# Revit family: Crealco Skyline Heavy Duty Sash Top Hung I
name_source: partatom
category: Windows
revit_build: Autodesk Revit 2014 (Build: 20130308_1515(x64)
units: mm (PartAtom-declared; Revit-internal decimal feet)

## types (24) — shared parameters
Corrected Mullion Configuration = 2 mm  [stored 0.00656168 ft]
Custom Sash Height = 525 mm
Description = Top Hung Type I Standard Sash Window
Frame Profile Thickness = 41 mm  [stored 0.134514 ft]
Heavy Duty Sash = Yes
Limit Fixed Pane Height Max = 3300 mm  [stored 10.8268 ft]
Limit Fixed Pane Height Min = 200 mm  [stored 0.656168 ft]
Limit Fixed Pane Width Max = 3000 mm  [stored 9.84252 ft]
Limit Fixed Pane Width Min = 200 mm  [stored 0.656168 ft]
Limit Sash Height Max = 1200 mm  [stored 3.93701 ft]
Limit Sash Height Min = 300 mm  [stored 0.984252 ft]
Limit Sash Width Max = 1500 mm  [stored 4.92126 ft]
Limit Sash Width Min = 300 mm  [stored 0.984252 ft]
Manufacturer = Crealco
Max System DG Unit Thickness = 25 mm  [stored 0.082021 ft]
Model = Skyline
Rough Width = 3 mm  [stored 0.00984252 ft]
Sash Side Gap = 44 mm
Standard Mullion Different = No
Standard Sash = No
URL = www.crealco.co.za
Wall Closure = By host
zero-valued in all types: Custom Frame Offset From Exterior

## per-type parameters (varying)
| type | Clearvue Insulated LowE SHGC Value | Clearvue Insulated LowE U Value | Clearvue Insulated SHGC Value | Clearvue Insulated U Value | Clearvue SHGC Value | Clearvue U Value | Custom Sash Width | Custom Windload | Custom Window Height | Custom Window Width | Energy Advantage SHGC Value | Energy Advantage U Value | Intruderprufe Insulated LowE SHGC Value | Intruderprufe Insulated LowE U Value | Intruderprufe Insulated SHGC Value | Intruderprufe Insulated U Value | Intruderprufe LowE SHGC Value | Intruderprufe LowE U Value | Intruderprufe SHGC Value | Intruderprufe U Value | Toughened Safety SHGC Value | Toughened Safety U Value |
| 1200 x 1500mm 1000Pa | 0.696 | 4.39 | 0.696 | 4.48 | 0.557 | 6.06 | 525 mm | 1000 mm  [stored 3.28084 ft] | 1490 mm  [stored 4.88845 ft] | 1190 mm  [stored 3.9042 ft] | 0.5 | 4.71 | 0.578 | 3.25 | 0.579 | 3.45 | 0.465 | 4.55 | 0.524 | 5.78 | 0.557 | 6.06 |
| 1200 x 1500mm 1500Pa | 0.696 | 4.39 | 0.696 | 4.48 | 0.557 | 6.06 | 525 mm | 1500 mm  [stored 4.92126 ft] | 1490 mm  [stored 4.88845 ft] | 1190 mm  [stored 3.9042 ft] | 0.5 | 4.71 | 0.578 | 3.25 | 0.579 | 3.45 | 0.465 | 4.55 | 0.524 | 5.78 | 0.557 | 6.06 |
| 1200 x 1500mm 2000Pa | 0.697 | 4.52 | 0.697 | 4.61 | 0.549 | 6.12 | 525 mm | 2000 mm  [stored 6.56168 ft] | 1490 mm  [stored 4.88845 ft] | 1190 mm  [stored 3.9042 ft] | 0.493 | 4.81 | 0.58 | 3.38 | 0.58 | 3.58 | 0.458 | 4.65 | 0.516 | 5.84 | 0.549 | 6.12 |
| 1500 x 1500mm 2000Pa | 0.728 | 4.69 | 0.728 | 4.76 | 0.597 | 6.08 | 525 mm | 2000 mm  [stored 6.56168 ft] | 1490 mm  [stored 4.88845 ft] | 1490 mm  [stored 4.88845 ft] | 0.535 | 4.64 | 0.605 | 3.37 | 0.605 | 3.53 | 0.497 | 4.48 | 0.561 | 5.82 | 0.597 | 6.08 |
| 1500 x 1500mm 1000Pa | 0.727 | 4.59 | 0.727 | 4.66 | 0.604 | 6.03 | 525 mm | 1000 mm  [stored 3.28084 ft] | 1490 mm  [stored 4.88845 ft] | 1490 mm  [stored 4.88845 ft] | 0.541 | 4.56 | 0.604 | 3.27 | 0.605 | 3.42 | 0.503 | 4.41 | 0.568 | 5.77 | 0.604 | 6.03 |
| 1500 x 1500mm 1500Pa | 0.727 | 4.59 | 0.727 | 4.66 | 0.604 | 6.03 | 525 mm | 1500 mm  [stored 4.92126 ft] | 1490 mm  [stored 4.88845 ft] | 1490 mm  [stored 4.88845 ft] | 0.541 | 4.56 | 0.604 | 3.27 | 0.605 | 3.42 | 0.503 | 4.41 | 0.568 | 5.77 | 0.604 | 6.03 |
| 1200 x 1800mm 1000Pa | 0.71 | 4.48 | 0.71 | 4.57 | 0.582 | 6.04 | 525 mm | 1000 mm  [stored 3.28084 ft] | 1790 mm  [stored 5.8727 ft] | 1190 mm  [stored 3.9042 ft] | 0.522 | 4.64 | 0.59 | 3.28 | 0.591 | 3.45 | 0.485 | 4.48 | 0.547 | 5.77 | 0.582 | 6.04 |
| 1200 x 1800mm 1500Pa | 0.711 | 4.62 | 0.711 | 4.7 | 0.569 | 6.12 | 525 mm | 1500 mm  [stored 4.92126 ft] | 1790 mm  [stored 5.8727 ft] | 1190 mm  [stored 3.9042 ft] | 0.511 | 4.76 | 0.591 | 3.41 | 0.592 | 3.57 | 0.475 | 4.59 | 0.535 | 5.84 | 0.569 | 6.12 |
| 1200 x 1800mm 2000Pa | 0.711 | 4.62 | 0.711 | 4.7 | 0.569 | 6.12 | 525 mm | 2000 mm  [stored 6.56168 ft] | 1790 mm  [stored 5.8727 ft] | 1190 mm  [stored 3.9042 ft] | 0.511 | 4.76 | 0.591 | 3.41 | 0.592 | 3.57 | 0.475 | 4.59 | 0.535 | 5.84 | 0.569 | 6.12 |
| 1500 x 1800mm 1000Pa | 0.739 | 4.79 | 0.739 | 4.86 | 0.615 | 6.08 | 525 mm | 1000 mm  [stored 3.28084 ft] | 1790 mm  [stored 5.8727 ft] | 1490 mm  [stored 4.88845 ft] | 0.551 | 4.59 | 0.614 | 3.4 | 0.615 | 3.53 | 0.512 | 4.43 | 0.578 | 5.82 | 0.615 | 6.08 |
| 1500 x 1800mm 1500Pa | 0.739 | 4.79 | 0.739 | 4.86 | 0.615 | 6.08 | 525 mm | 1500 mm  [stored 4.92126 ft] | 1790 mm  [stored 5.8727 ft] | 1490 mm  [stored 4.88845 ft] | 0.551 | 4.59 | 0.614 | 3.4 | 0.615 | 3.53 | 0.512 | 4.43 | 0.578 | 5.82 | 0.615 | 6.08 |
| 1500 x 1800mm 2000Pa | 0.739 | 4.79 | 0.739 | 4.86 | 0.615 | 6.08 | 525 mm | 2000 mm  [stored 6.56168 ft] | 1790 mm  [stored 5.8727 ft] | 1490 mm  [stored 4.88845 ft] | 0.551 | 4.59 | 0.614 | 3.4 | 0.615 | 3.53 | 0.512 | 4.43 | 0.578 | 5.82 | 0.615 | 6.08 |
| 1800 x 1500mm 1000Pa | 0.72 | 4.59 | 0.72 | 4.67 | 0.606 | 6.03 | 825 mm | 1000 mm  [stored 3.28084 ft] | 1490 mm  [stored 4.88845 ft] | 1790 mm  [stored 5.8727 ft] | 0.543 | 4.52 | 0.599 | 3.29 | 0.6 | 3.48 | 0.505 | 4.37 | 0.57 | 5.75 | 0.606 | 6.03 |
| 1800 x 1500mm 1500Pa | 0.721 | 4.68 | 0.721 | 4.76 | 0.6 | 6.08 | 825 mm | 1500 mm  [stored 4.92126 ft] | 1490 mm  [stored 4.88845 ft] | 1790 mm  [stored 5.8727 ft] | 0.538 | 4.58 | 0.599 | 3.38 | 0.6 | 3.57 | 0.5 | 4.44 | 0.564 | 5.79 | 0.6 | 6.08 |
| 1800 x 1500mm 2000Pa | 0.721 | 4.68 | 0.721 | 4.76 | 0.6 | 6.08 | 825 mm | 2000 mm  [stored 6.56168 ft] | 1490 mm  [stored 4.88845 ft] | 1790 mm  [stored 5.8727 ft] | 0.538 | 4.58 | 0.599 | 3.38 | 0.6 | 3.57 | 0.5 | 4.44 | 0.564 | 5.79 | 0.6 | 6.08 |
| 2400 x 1500mm 1000Pa | 0.753 | 4.79 | 0.753 | 4.85 | 0.651 | 6.01 | 825 mm | 1000 mm  [stored 3.28084 ft] | 1490 mm  [stored 4.88845 ft] | 2390 mm  [stored 7.84121 ft] | 0.583 | 4.38 | 0.625 | 3.3 | 0.626 | 3.44 | 0.542 | 4.24 | 0.613 | 5.75 | 0.651 | 6.01 |
| 2400 x 1500mm 1500Pa | 0.754 | 4.86 | 0.754 | 4.91 | 0.647 | 6.04 | 825 mm | 1500 mm  [stored 4.92126 ft] | 1490 mm  [stored 4.88845 ft] | 2390 mm  [stored 7.84121 ft] | 0.579 | 4.43 | 0.626 | 3.36 | 0.627 | 3.51 | 0.538 | 4.29 | 0.608 | 5.78 | 0.647 | 6.04 |
| 2400 x 1500mm 2000Pa | 0.754 | 4.86 | 0.754 | 4.91 | 0.647 | 6.04 | 825 mm | 2000 mm  [stored 6.56168 ft] | 1490 mm  [stored 4.88845 ft] | 2390 mm  [stored 7.84121 ft] | 0.579 | 4.43 | 0.626 | 3.36 | 0.627 | 3.51 | 0.538 | 4.29 | 0.608 | 5.78 | 0.647 | 6.04 |
| 1800 x 1800mm 1000Pa | 0.735 | 4.8 | 0.735 | 4.86 | 0.622 | 6.07 | 825 mm | 1000 mm  [stored 3.28084 ft] | 1790 mm  [stored 5.8727 ft] | 1790 mm  [stored 5.8727 ft] | 0.557 | 4.53 | 0.611 | 3.41 | 0.612 | 3.57 | 0.518 | 4.38 | 0.585 | 5.79 | 0.622 | 6.07 |
| 1800 x 1800mm 1500Pa | 0.735 | 4.8 | 0.735 | 4.86 | 0.622 | 6.07 | 825 mm | 1500 mm  [stored 4.92126 ft] | 1790 mm  [stored 5.8727 ft] | 1790 mm  [stored 5.8727 ft] | 0.557 | 4.53 | 0.611 | 3.41 | 0.612 | 3.57 | 0.518 | 4.38 | 0.585 | 5.79 | 0.622 | 6.07 |
| 1800 x 1800mm 2000Pa | 0.735 | 4.8 | 0.735 | 4.86 | 0.622 | 6.07 | 825 mm | 2000 mm  [stored 6.56168 ft] | 1790 mm  [stored 5.8727 ft] | 1790 mm  [stored 5.8727 ft] | 0.557 | 4.53 | 0.611 | 3.41 | 0.612 | 3.57 | 0.518 | 4.38 | 0.585 | 5.79 | 0.622 | 6.07 |
| 2400 x 1800mm 1000Pa | 0.764 | 4.96 | 0.764 | 5.01 | 0.666 | 6.03 | 825 mm | 1000 mm  [stored 3.28084 ft] | 1790 mm  [stored 5.8727 ft] | 2390 mm  [stored 7.84121 ft] | 0.596 | 4.37 | 0.634 | 3.4 | 0.635 | 3.52 | 0.554 | 4.23 | 0.626 | 5.78 | 0.666 | 6.03 |
| 2400 x 1800mm 1500Pa | 0.764 | 4.96 | 0.764 | 5.01 | 0.666 | 6.03 | 825 mm | 1500 mm  [stored 4.92126 ft] | 1790 mm  [stored 5.8727 ft] | 2390 mm  [stored 7.84121 ft] | 0.596 | 4.37 | 0.634 | 3.4 | 0.635 | 3.52 | 0.554 | 4.23 | 0.626 | 5.78 | 0.666 | 6.03 |
| 2400 x 1800mm 2000Pa | 0.764 | 4.96 | 0.764 | 5.01 | 0.666 | 6.03 | 825 mm | 2000 mm  [stored 6.56168 ft] | 1790 mm  [stored 5.8727 ft] | 2390 mm  [stored 7.84121 ft] | 0.596 | 4.37 | 0.634 | 3.4 | 0.635 | 3.52 | 0.554 | 4.23 | 0.626 | 5.78 | 0.666 | 6.03 |

note: [stored X ft] marks values corroborated as IEEE doubles in the binary element streams (Revit-internal decimal feet)

## geometry (parser evidence)
native form markers: Sweep x15
no freeform markers — native parametric forms only
